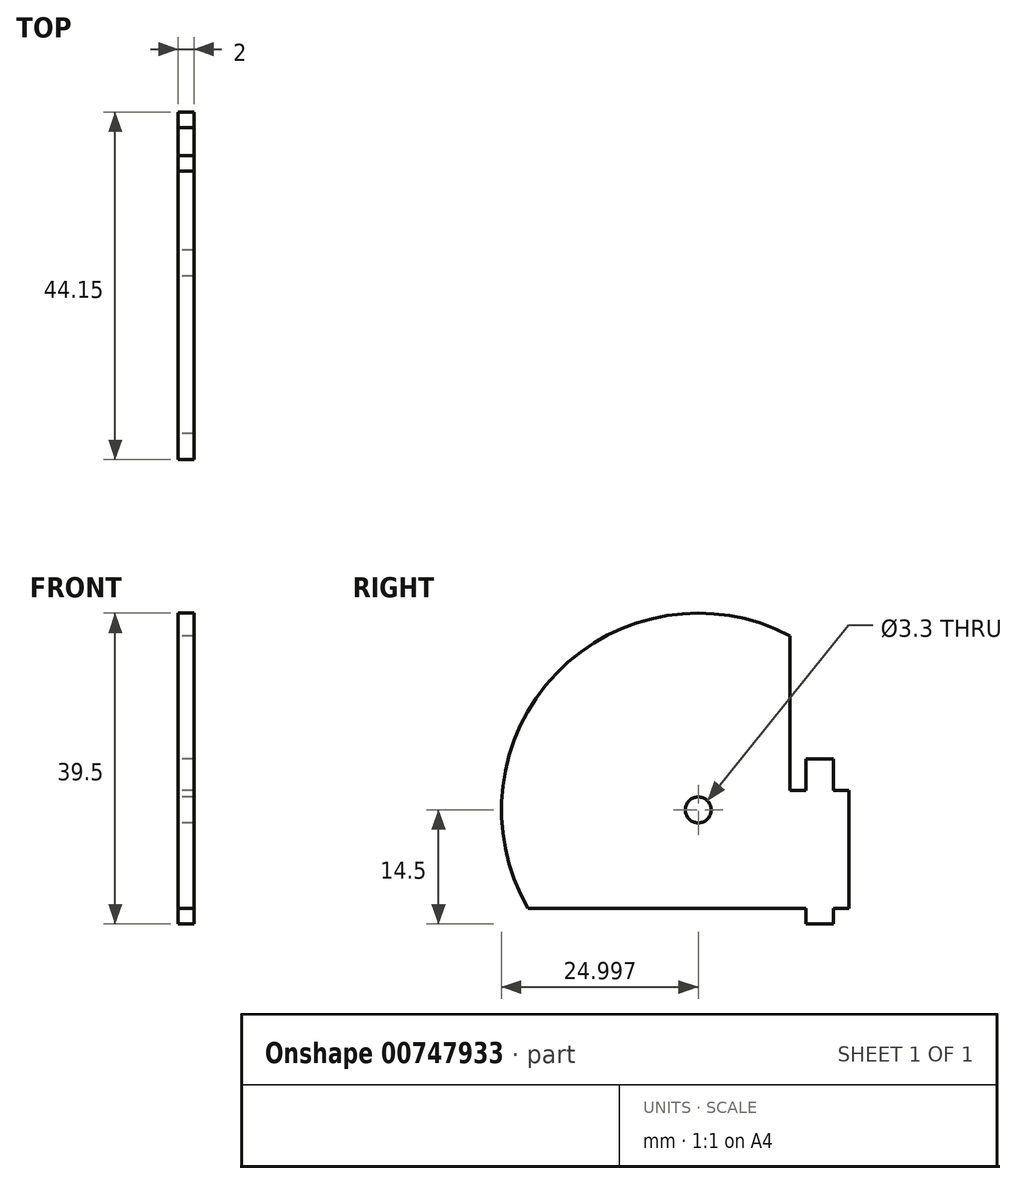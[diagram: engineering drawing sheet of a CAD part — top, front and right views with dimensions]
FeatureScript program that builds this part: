
annotation { "Feature Type Name" : "Feature", "Feature Type Description" : "" }
export const myFeature = defineFeature(function(context is Context, id is Id, definition is map)
    precondition{}
    {
        {
            var Q0;
            Q0=qCreatedBy(makeId("Right.planeOp"),FACE);
            var sketch = newSketch(context, id + "F0", { "sketchPlane" : qUnion([Q0])});
            skLineSegment(sketch, "E0", {"start": v(0, 0) * mm, "end": v(-31, 0) * mm, "construction": true});
            skLineSegment(sketch, "E1", {"start": v(-31, 0) * mm, "end": v(-31, 4) * mm});
            skLineSegment(sketch, "E2", {"start": v(0, 0) * mm, "end": v(-23.5, 0) * mm, "construction": true});
            skLineSegment(sketch, "E3", {"start": v(-31, 0) * mm, "end": v(-29, 0) * mm});
            skLineSegment(sketch, "E4", {"start": v(-23.5, 0) * mm, "end": v(-25.5, 0) * mm});
            skLineSegment(sketch, "E5", {"start": v(-25.5, 0) * mm, "end": v(-25.5, 4) * mm});
            skLineSegment(sketch, "E6", {"start": v(-25.5, 4) * mm, "end": v(-29, 4) * mm});
            skLineSegment(sketch, "E7", {"start": v(-29, 4) * mm, "end": v(-29, 0) * mm});
            skLineSegment(sketch, "E8", {"start": v(-23.5, 0) * mm, "end": v(-23.5, -15) * mm});
            skLineSegment(sketch, "E9", {"start": v(-42.65, -2.5) * mm, "end": v(-42.65, 22.5) * mm, "construction": true});
            skLineSegment(sketch, "E10", {"start": v(-42.65, -2.5) * mm, "end": v(-67.65, -2.5) * mm, "construction": true});
            skLineSegment(sketch, "E11", {"start": v(-42.65, -2.5) * mm, "end": v(-42.65, -15) * mm, "construction": true});
            skLineSegment(sketch, "E12", {"start": v(-42.65, -2.5) * mm, "end": v(-31.83, 3.75) * mm, "construction": true});
            skLineSegment(sketch, "E13", {"start": v(-23.5, -15) * mm, "end": v(-25.5, -15) * mm});
            skLineSegment(sketch, "E14", {"start": v(-25.5, -15) * mm, "end": v(-25.5, -17) * mm});
            skLineSegment(sketch, "E15", {"start": v(-25.5, -17) * mm, "end": v(-29, -17) * mm});
            skLineSegment(sketch, "E16", {"start": v(-29, -17) * mm, "end": v(-29, -15) * mm});
            skLineSegment(sketch, "E17", {"start": v(-29, -15) * mm, "end": v(-42.65, -15) * mm});
            skCircle(sketch, "E18", {"center": v(-42.65, -2.5) * mm, "radius": 1.65 * mm});
            skLineSegment(sketch, "E19", {"start": v(-42.65, -15) * mm, "end": v(-64.3, -15) * mm});
            skLineSegment(sketch, "E20", {"start": v(-31, 19.62) * mm, "end": v(-31, 4) * mm});
            skArc(sketch, "E21", {"start": v(-31, 19.62) * mm, "mid": v(-60.67, 14.83) * mm, "end": v(-64.3, -15) * mm});
            skPoint(sketch, "E22.orphan", {"position": v(-67.65, 22.5) * mm});
            skSolve(sketch);
        }
        {
            var Q0;
            Q0 = qSketchRegion(id + "F0", true);
            extrude(context, id + "F1", {"entities" : qUnion([Q0]), "depth" : 2 * mm, "offsetDistance" : 25 * mm});
        }
    });
